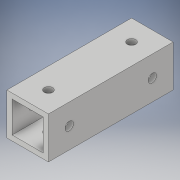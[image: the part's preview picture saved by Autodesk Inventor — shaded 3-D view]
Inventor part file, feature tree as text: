
AUTODESK INVENTOR PART (.ipt)
format: ipt  version: 2018 (Build 220112000, 112)  size: 126,464 bytes
history: native  units: in
note: dims shown in document units (in); Inventor stores cm internally (conversion verified against a paired STEP export)
features: extrude x3, sketch x3
ambient origin geometry x8: Origin, YZ Plane, XZ Plane, XY Plane, X Axis, Y Axis, Z Axis, Center Point
bodies: Solid1 (feature_tree)
feature tree (6):
  extrude  "Extrusion1"  Depth=1.0in
  extrude  "Extrusion2"  Depth=3.0in TaperAngle=0.0deg
  extrude  "Extrusion3"  Depth=3.0in
  sketch  "Sketch1"  dims[d0=1.0in d1=1.0in]
  sketch  "Sketch2"  dims[d2=0.125in d3=3.0in d4=0.0in]
  sketch  "Sketch3"  dims[d5=0.5in d6=0.5in d7=0.2031in d8=3.0in d9=0.0in d10=0.5in d11=0.5in d12=0.2031in d13=3.0in d14=0.0in]
